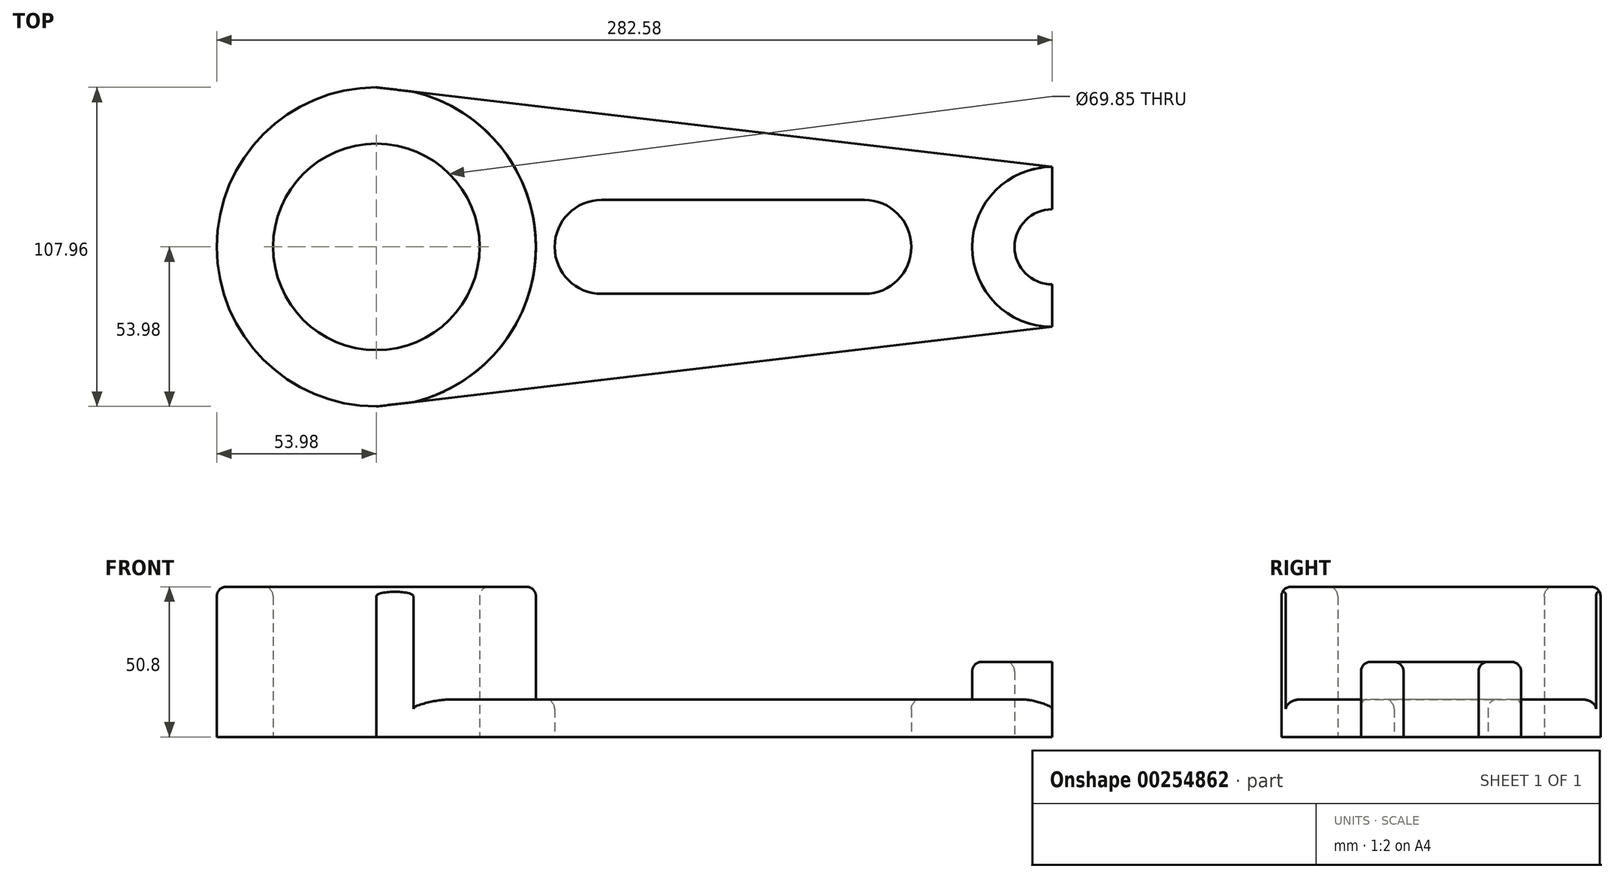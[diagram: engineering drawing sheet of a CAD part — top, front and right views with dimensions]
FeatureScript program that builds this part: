
annotation { "Feature Type Name" : "Feature", "Feature Type Description" : "" }
export const myFeature = defineFeature(function(context is Context, id is Id, definition is map)
    precondition{}
    {
        {
            var Q0;
            Q0=qCreatedBy(makeId("Top.planeOp"),FACE);
            var sketch = newSketch(context, id + "F0", { "sketchPlane" : qUnion([Q0])});
            skCircle(sketch, "E0", {"center": v(-76.2, 0) * mm, "radius": 53.98 * mm});
            skCircle(sketch, "E1", {"center": v(-76.2, 0) * mm, "radius": 34.93 * mm});
            skCircle(sketch, "E2", {"center": v(152.4, 0) * mm, "radius": 27.05 * mm});
            skCircle(sketch, "E3", {"center": v(152.4, 0) * mm, "radius": 12.7 * mm});
            skCircle(sketch, "E4", {"center": v(0, 0) * mm, "radius": 15.88 * mm});
            skCircle(sketch, "E5", {"center": v(88.9, 0) * mm, "radius": 15.88 * mm});
            skLineSegment(sketch, "E6", {"start": v(0, 0) * mm, "end": v(0, 15.88) * mm});
            skLineSegment(sketch, "E7", {"start": v(0, 15.88) * mm, "end": v(0, 0) * mm});
            skLineSegment(sketch, "E8", {"start": v(0, 0) * mm, "end": v(0, -15.88) * mm});
            skLineSegment(sketch, "E9", {"start": v(88.9, 15.88) * mm, "end": v(88.9, -15.88) * mm});
            skLineSegment(sketch, "E10", {"start": v(-76.2, 53.98) * mm, "end": v(-76.2, -53.98) * mm});
            skLineSegment(sketch, "E11", {"start": v(0, -15.88) * mm, "end": v(88.9, -15.88) * mm});
            skLineSegment(sketch, "E12", {"start": v(0, 15.88) * mm, "end": v(88.9, 15.88) * mm});
            skLineSegment(sketch, "E13", {"start": v(-76.2, 0) * mm, "end": v(152.4, 0) * mm});
            skLineSegment(sketch, "E14", {"start": v(152.4, 27.05) * mm, "end": v(152.4, -27.05) * mm});
            skLineSegment(sketch, "E15", {"start": v(-76.2, 53.97) * mm, "end": v(152.4, 27.05) * mm});
            skLineSegment(sketch, "E16", {"start": v(-76.2, -53.97) * mm, "end": v(152.4, -27.05) * mm});
            skSolve(sketch);
        }
        {
            var Q0;
            {var subQ0=sQuery(id+"F0.wireOp",EDGE,"E12");Q0=makeQuery(id+"F0.imprint","IMPRINT",FACE,{"disambiguationData":[TD([[makeQuery(id+"F0.imprint","IMPRINT",EDGE,{"derivedFrom":subQ0}),1.0]])]});}
            var Q1;
            {var subQ0=sQuery(id+"F0.wireOp",EDGE,"E11");Q1=makeQuery(id+"F0.imprint","IMPRINT",FACE,{"disambiguationData":[TD([[makeQuery(id+"F0.imprint","IMPRINT",EDGE,{"derivedFrom":subQ0}),-1.0]])]});}
            extrude(context, id + "F1", {"entities" : qUnion([Q0, Q1]), "depth" : 12.7 * mm});
        }
        {
            var Q0;
            {var subQ0=sQuery(id+"F0.wireOp",EDGE,"E10");var subQ4=sQuery(id+"F0.wireOp",EDGE,"E1");var subQ5=makeQuery(id+"F0.imprint","INTERSECT",VERTEX,{"disambiguationData":[OD(0.0)],"derivedFrom":[subQ4,subQ0]});Q0=makeQuery(id+"F0.imprint","IMPRINT",FACE,{"disambiguationData":[TD([[makeQuery(id+"F0.imprint","IMPRINT",EDGE,{"disambiguationData":[TD([[subQ5,-1.0]])],"derivedFrom":subQ4}),-1.0]])]});}
            var Q1;
            {var subQ0=sQuery(id+"F0.wireOp",EDGE,"E15");var subQ2=sQuery(id+"F0.wireOp",EDGE,"E0");var subQ9=makeQuery(id+"F0.imprint","INTERSECT",VERTEX,{"derivedFrom":[subQ2,subQ0]});Q1=makeQuery(id+"F0.imprint","IMPRINT",FACE,{"disambiguationData":[TD([[makeQuery(id+"F0.imprint","IMPRINT",EDGE,{"disambiguationData":[TD([[subQ9,1.0]])],"derivedFrom":subQ2}),1.0]])]});}
            var Q2;
            {var subQ1=sQuery(id+"F0.wireOp",EDGE,"E0");var subQ5=sQuery(id+"F0.wireOp",EDGE,"E16");var subQ9=makeQuery(id+"F0.imprint","INTERSECT",VERTEX,{"derivedFrom":[subQ1,subQ5]});Q2=makeQuery(id+"F0.imprint","IMPRINT",FACE,{"disambiguationData":[TD([[makeQuery(id+"F0.imprint","IMPRINT",EDGE,{"disambiguationData":[TD([[subQ9,-1.0]])],"derivedFrom":subQ1}),1.0]])]});}
            extrude(context, id + "F2", {"entities" : qUnion([Q0, Q1, Q2]), "operationType" : NewBodyOperationType.ADD, "depth" : 50.8 * mm});
        }
        {
            var Q0;
            {var subQ3=sQuery(id+"F0.wireOp",EDGE,"E13");var subQ5=sQuery(id+"F0.wireOp",EDGE,"E3");var subQ6=makeQuery(id+"F0.imprint","INTERSECT",VERTEX,{"derivedFrom":[subQ5,subQ3]});Q0=makeQuery(id+"F0.imprint","IMPRINT",FACE,{"disambiguationData":[TD([[makeQuery(id+"F0.imprint","IMPRINT",EDGE,{"disambiguationData":[TD([[subQ6,1.0]])],"derivedFrom":subQ5}),-1.0]])]});}
            var Q1;
            {var subQ3=sQuery(id+"F0.wireOp",EDGE,"E13");var subQ5=sQuery(id+"F0.wireOp",EDGE,"E3");var subQ6=makeQuery(id+"F0.imprint","INTERSECT",VERTEX,{"derivedFrom":[subQ5,subQ3]});Q1=makeQuery(id+"F0.imprint","IMPRINT",FACE,{"disambiguationData":[TD([[makeQuery(id+"F0.imprint","IMPRINT",EDGE,{"disambiguationData":[TD([[subQ6,-1.0]])],"derivedFrom":subQ5}),-1.0]])]});}
            var Q2;
            {var subQ0=sQuery(id+"F0.wireOp",EDGE,"E14");var subQ4=sQuery(id+"F0.wireOp",EDGE,"E3");var subQ5=makeQuery(id+"F0.imprint","INTERSECT",VERTEX,{"disambiguationData":[OD(0.0)],"derivedFrom":[subQ4,subQ0]});Q2=makeQuery(id+"F0.imprint","IMPRINT",FACE,{"disambiguationData":[TD([[makeQuery(id+"F0.imprint","IMPRINT",EDGE,{"disambiguationData":[TD([[subQ5,1.0]])],"derivedFrom":subQ4}),-1.0]])]});}
            extrude(context, id + "F3", {"entities" : qUnion([Q0, Q1, Q2]), "operationType" : NewBodyOperationType.ADD, "depth" : 25.4 * mm});
        }
        {
            var Q0;
            Q0=makeQuery(id+"F2.opExtrude","CAP_EDGE",EDGE,{"disambiguationData":[OSD([sQuery(id+"F0.wireOp",EDGE,"E1")])],"isStart":false});
            var Q1;
            {var subQ0=sQuery(id+"F0.wireOp",EDGE,"E0");Q1=makeQuery(id+"F2.opExtrude","CAP_EDGE",EDGE,{"disambiguationData":[OSD([subQ0]),TDD([makeQuery(id+"F0.imprint","IMPRINT",EDGE,{"disambiguationData":[TD([[makeQuery(id+"F0.imprint","INTERSECT",VERTEX,{"derivedFrom":[subQ0,sQuery(id+"F0.wireOp",EDGE,"E15")]}),1.0]])],"derivedFrom":subQ0}),makeQuery(id+"F0.imprint","IMPRINT",EDGE,{"disambiguationData":[TD([[makeQuery(id+"F0.imprint","INTERSECT",VERTEX,{"derivedFrom":[subQ0,sQuery(id+"F0.wireOp",EDGE,"E16")]}),-1.0]])],"derivedFrom":subQ0})])],"isStart":false});}
            var Q2;
            Q2=makeQuery(id+"F1.opExtrude","CAP_EDGE",EDGE,{"disambiguationData":[OSD([sQuery(id+"F0.wireOp",EDGE,"E15")])],"isStart":false});
            var Q3;
            Q3=makeQuery(id+"F1.opExtrude","CAP_EDGE",EDGE,{"disambiguationData":[OSD([sQuery(id+"F0.wireOp",EDGE,"E12")])],"isStart":false});
            var Q4;
            Q4=makeQuery(id+"F1.opExtrude","CAP_EDGE",EDGE,{"disambiguationData":[OSD([sQuery(id+"F0.wireOp",EDGE,"E4")])],"isStart":false});
            var Q5;
            Q5=makeQuery(id+"F1.opExtrude","CAP_EDGE",EDGE,{"disambiguationData":[OSD([sQuery(id+"F0.wireOp",EDGE,"E16")])],"isStart":false});
            var Q6;
            Q6=makeQuery(id+"F3.opExtrude","CAP_EDGE",EDGE,{"disambiguationData":[OSD([sQuery(id+"F0.wireOp",EDGE,"E2")])],"isStart":false});
            var Q7;
            Q7=makeQuery(id+"F3.opExtrude","CAP_EDGE",EDGE,{"disambiguationData":[OSD([sQuery(id+"F0.wireOp",EDGE,"E3")])],"isStart":false});
            fillet(context, id + "F4", {"entities" : qUnion([Q0, Q1, Q2, Q3, Q4, Q5, Q6, Q7]), "radius" : 3.17 * mm, "tangentPropagation" : true, "allowEdgeOverflow" : false});
        }
    });
